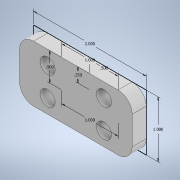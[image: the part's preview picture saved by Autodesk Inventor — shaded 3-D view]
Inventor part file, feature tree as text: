
AUTODESK INVENTOR PART (.ipt)
format: ipt  version: 2020 (Build 240168000, 168)  size: 121,856 bytes
history: native  units: in
note: dims shown in document units (in); Inventor stores cm internally (conversion verified against a paired STEP export)
features: sketch x1, extrude x1, hole x1, fillet x1
ambient origin geometry x8: Origin, YZ Plane, XZ Plane, XY Plane, X Axis, Y Axis, Z Axis, Center Point
bodies: Solid1 (feature_tree)
feature tree (4):
  sketch  "Sketch1"  dims[d0=2.0in d1=1.0in d2=0.25in d3=0.5in d4=1.0in d5=0.5in d6=1.0in d7=0.25in d8=0.0in d9=0.266in d10=0.75in d11=0.438in d12=0.25in d13=0.5635in d14=1.0in d15=0.8108in d16=0.25in]
  extrude  "Extrusion1"  Depth=1.0in
  hole  "Hole1"  [1 undecoded]
  fillet  "Fillet1"  Radius=0.5in
note: 1 required parameter value undecoded (feature->parameter linkage not recoverable at this tier; creation-order binding heuristic only, values carry confidence <= 0.55)
